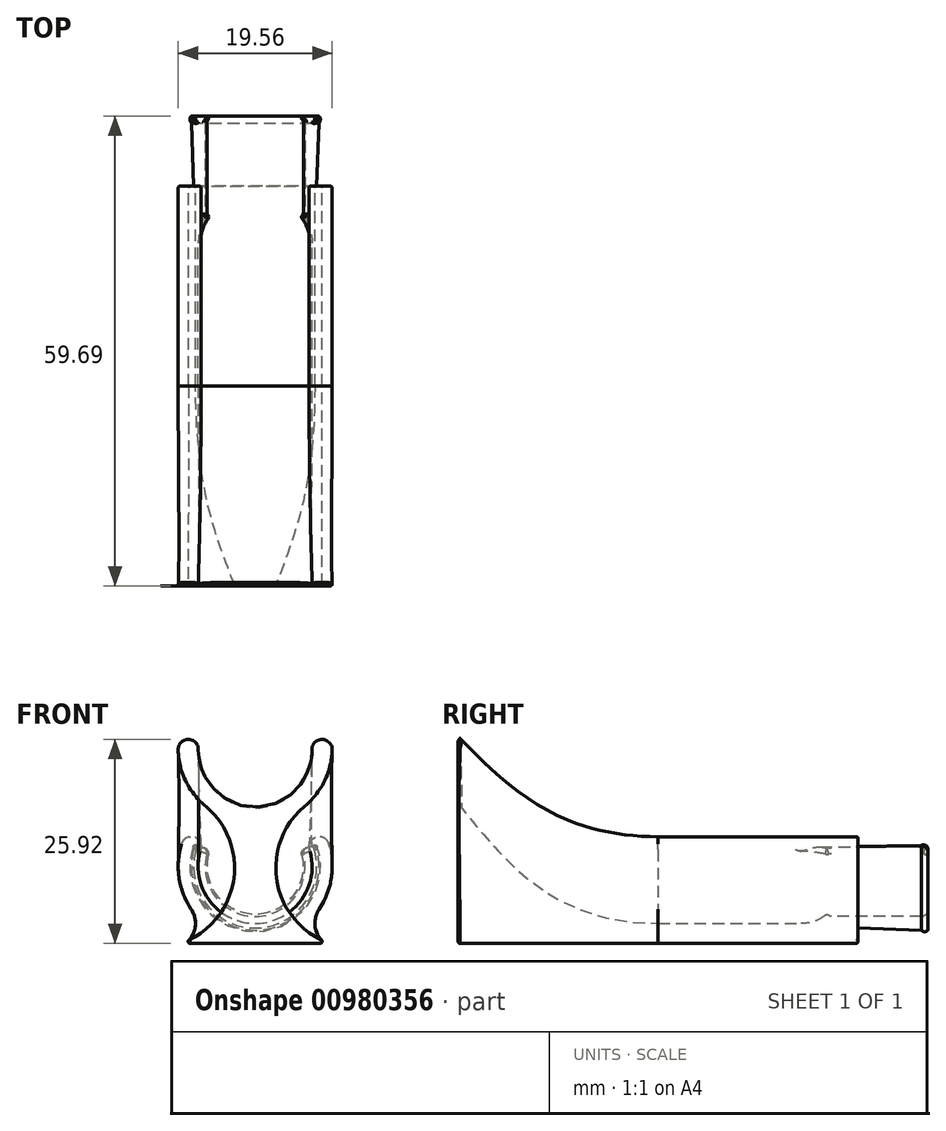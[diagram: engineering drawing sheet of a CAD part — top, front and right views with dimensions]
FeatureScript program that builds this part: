
annotation { "Feature Type Name" : "Feature", "Feature Type Description" : "" }
export const myFeature = defineFeature(function(context is Context, id is Id, definition is map)
    precondition{}
    {
        {
            var Q0;
            Q0=qCreatedBy(makeId("Front.planeOp"),FACE);
            var sketch = newSketch(context, id + "F0", { "sketchPlane" : qUnion([Q0])});
            skLineSegment(sketch, "E0", {"start": v(0, 0) * mm, "end": v(0, 2.54) * mm, "construction": true});
            skLineSegment(sketch, "E1", {"start": v(0, 0) * mm, "end": v(-8.23, 0) * mm});
            skArc(sketch, "E2", {"start": v(-6.91, 11.92) * mm, "mid": v(-5.83, 5.48) * mm, "end": v(0, 2.54) * mm});
            skArc(sketch, "E3", {"start": v(-6.91, 11.92) * mm, "mid": v(-7.75, 13.5) * mm, "end": v(-9.34, 12.67) * mm});
            skArc(sketch, "E4", {"start": v(-9.34, 12.67) * mm, "mid": v(-9.68, 8.37) * mm, "end": v(-8.12, 4.33) * mm});
            skArc(sketch, "E5", {"start": v(-8.42, 0.43) * mm, "mid": v(-7.6, 2.33) * mm, "end": v(-8.12, 4.33) * mm});
            skPoint(sketch, "E6.visualSharp", {"position": v(-8.9, 0) * mm});
            skArc(sketch, "E6.filletArc", {"start": v(-8.42, 0.43) * mm, "mid": v(-8.46, 0.15) * mm, "end": v(-8.23, 0) * mm});
            skPoint(sketch, "E7", {"position": v(-7.24, 9.78) * mm});
            skPoint(sketch, "E8", {"position": v(-6.86, 12.3) * mm});
            skArc(sketch, "E9.MirrorCS", {"start": v(6.91, 11.92) * mm, "mid": v(5.83, 5.48) * mm, "end": v(0, 2.54) * mm});
            skArc(sketch, "E10.MirrorCS", {"start": v(6.91, 11.92) * mm, "mid": v(7.75, 13.5) * mm, "end": v(9.34, 12.67) * mm});
            skArc(sketch, "E11.MirrorCS", {"start": v(9.34, 12.67) * mm, "mid": v(9.68, 8.37) * mm, "end": v(8.12, 4.33) * mm});
            skArc(sketch, "E12.MirrorCS", {"start": v(8.42, 0.43) * mm, "mid": v(7.6, 2.33) * mm, "end": v(8.12, 4.33) * mm});
            skLineSegment(sketch, "E13.MirrorCS", {"start": v(0, 0) * mm, "end": v(8.23, 0) * mm});
            skArc(sketch, "E14.MirrorCS", {"start": v(8.42, 0.43) * mm, "mid": v(8.46, 0.15) * mm, "end": v(8.23, 0) * mm});
            skSolve(sketch);
        }
        {
            var Q0;
            Q0=qSketchRegion(id+"F0",true);
            extrude(context, id + "F1", {"entities" : qUnion([Q0]), "depth" : 25.4 * mm, "offsetDistance" : 25.4 * mm});
        }
        {
            var Q0;
            Q0=makeQuery(id+"F1.opExtrude","CAP_FACE",FACE,{"disambiguationData":[OSD([sQuery(id+"F0.wireOp",EDGE,"E1"),sQuery(id+"F0.wireOp",EDGE,"E2"),sQuery(id+"F0.wireOp",EDGE,"E3"),sQuery(id+"F0.wireOp",EDGE,"E4"),sQuery(id+"F0.wireOp",EDGE,"E5"),sQuery(id+"F0.wireOp",EDGE,"E6.filletArc"),sQuery(id+"F0.wireOp",EDGE,"E9.MirrorCS"),sQuery(id+"F0.wireOp",EDGE,"E10.MirrorCS"),sQuery(id+"F0.wireOp",EDGE,"E11.MirrorCS"),sQuery(id+"F0.wireOp",EDGE,"E12.MirrorCS"),sQuery(id+"F0.wireOp",EDGE,"E13.MirrorCS"),sQuery(id+"F0.wireOp",EDGE,"E14.MirrorCS")])],"isStart":false});
            cPlane(context, id + "F2", {"entities" : qUnion([Q0]), "cplaneType" : CPlaneType.OFFSET, "offset" : 25.4 * mm, "width" : 152.4 * mm, "height" : 152.4 * mm});
        }
        {
            var Q0;
            Q0=qCreatedBy(id+"F2.planeOp",FACE);
            var sketch = newSketch(context, id + "F3", { "sketchPlane" : qUnion([Q0])});
            skLineSegment(sketch, "E15", {"start": v(0, 0) * mm, "end": v(0, 17.78) * mm, "construction": true});
            skLineSegment(sketch, "E16", {"start": v(8.26, 0) * mm, "end": v(-8.26, 0) * mm});
            skArc(sketch, "E17", {"start": v(-7.24, 25.02) * mm, "mid": v(0, 17.78) * mm, "end": v(7.24, 25.02) * mm});
            skArc(sketch, "E18", {"start": v(-7.24, 25.02) * mm, "mid": v(-8.5, 26.29) * mm, "end": v(-9.78, 25.02) * mm});
            skArc(sketch, "E19", {"start": v(-9.78, 25.02) * mm, "mid": v(-8.85, 20.86) * mm, "end": v(-6.24, 17.49) * mm});
            skArc(sketch, "E20", {"start": v(-8.36, 0.48) * mm, "mid": v(-2.64, 8.4) * mm, "end": v(-6.24, 17.49) * mm});
            skArc(sketch, "E21.filletArc", {"start": v(-8.36, 0.48) * mm, "mid": v(-8.5, 0.2) * mm, "end": v(-8.26, 0) * mm});
            skPoint(sketch, "E22", {"position": v(-7.24, 25.02) * mm});
            skArc(sketch, "E23.MirrorCS", {"start": v(7.24, 25.02) * mm, "mid": v(8.5, 26.29) * mm, "end": v(9.78, 25.02) * mm});
            skArc(sketch, "E24.MirrorCS", {"start": v(9.78, 25.02) * mm, "mid": v(8.85, 20.86) * mm, "end": v(6.24, 17.49) * mm});
            skArc(sketch, "E25.MirrorCS", {"start": v(8.36, 0.48) * mm, "mid": v(2.64, 8.4) * mm, "end": v(6.24, 17.49) * mm});
            skArc(sketch, "E26.MirrorCS", {"start": v(8.36, 0.48) * mm, "mid": v(8.5, 0.2) * mm, "end": v(8.26, 0) * mm});
            skSolve(sketch);
        }
        {
            var Q1;
            Q1=makeQuery(id+"F3.imprint","IMPRINT",FACE,{"disambiguationData":[TD([[makeQuery(id+"F3.imprint","IMPRINT",EDGE,{"derivedFrom":sQuery(id+"F3.wireOp",EDGE,"E16")}),-1.0]])]});
            var Q2;
            Q2=makeQuery(id+"F1.opExtrude","CAP_FACE",FACE,{"disambiguationData":[OSD([sQuery(id+"F0.wireOp",EDGE,"E1"),sQuery(id+"F0.wireOp",EDGE,"E2"),sQuery(id+"F0.wireOp",EDGE,"E3"),sQuery(id+"F0.wireOp",EDGE,"E4"),sQuery(id+"F0.wireOp",EDGE,"E5"),sQuery(id+"F0.wireOp",EDGE,"E6.filletArc"),sQuery(id+"F0.wireOp",EDGE,"E9.MirrorCS"),sQuery(id+"F0.wireOp",EDGE,"E10.MirrorCS"),sQuery(id+"F0.wireOp",EDGE,"E11.MirrorCS"),sQuery(id+"F0.wireOp",EDGE,"E12.MirrorCS"),sQuery(id+"F0.wireOp",EDGE,"E13.MirrorCS"),sQuery(id+"F0.wireOp",EDGE,"E14.MirrorCS")])],"isStart":false});
            loft(context, id + "F4", {"operationType" : NewBodyOperationType.ADD, "endCondition" : LoftEndDerivativeType.MATCH_TANGENT, "endMagnitude" : 1.5, "sheetProfilesArray" : [{ "sheetProfileEntities" : qUnion([Q1]) }, { "sheetProfileEntities" : qUnion([Q2]) }]});
        }
        {
            var Q0;
            Q0=makeQuery(id+"F4.opLoft","MID_CAP_EDGE",EDGE,{"disambiguationData":[OSD([sQuery(id+"F3.wireOp",EDGE,"E17"),sQuery(id+"F3.wireOp",EDGE,"E18"),sQuery(id+"F3.wireOp",EDGE,"E23.MirrorCS")])],"capPos":0.0});
            fillet(context, id + "F5", {"entities" : qUnion([Q0]), "radius" : 0.25 * mm, "tangentPropagation" : true, "allowEdgeOverflow" : false});
        }
        {
            var Q0;
            Q0=qCreatedBy(makeId("Right.planeOp"),FACE);
            var sketch = newSketch(context, id + "F6", { "sketchPlane" : qUnion([Q0])});
            skLineSegment(sketch, "E27", {"start": v(0, 9.78) * mm, "end": v(9.62, 9.78) * mm, "construction": true});
            skLineSegment(sketch, "E28", {"start": v(-4.19, 2.1) * mm, "end": v(8.02, 1.68) * mm});
            skLineSegment(sketch, "E29", {"start": v(-4.19, 2.1) * mm, "end": v(-4.19, 3.43) * mm});
            skLineSegment(sketch, "E30", {"start": v(-3.37, 3.43) * mm, "end": v(8.07, 3.43) * mm});
            skLineSegment(sketch, "E31", {"start": v(8.9, 3.43) * mm, "end": v(8.9, 1.65) * mm});
            skArc(sketch, "E32", {"start": v(8.9, 3.43) * mm, "mid": v(8.73, 3.67) * mm, "end": v(8.45, 3.6) * mm});
            skArc(sketch, "E33", {"start": v(-3.75, 3.6) * mm, "mid": v(-4.03, 3.67) * mm, "end": v(-4.19, 3.43) * mm});
            skPoint(sketch, "E34.visualSharp", {"position": v(-3.68, 3.43) * mm});
            skArc(sketch, "E34.filletArc", {"start": v(-3.75, 3.6) * mm, "mid": v(-3.57, 3.47) * mm, "end": v(-3.37, 3.43) * mm});
            skPoint(sketch, "E35.visualSharp", {"position": v(8.38, 3.43) * mm});
            skArc(sketch, "E35.filletArc", {"start": v(8.07, 3.43) * mm, "mid": v(8.28, 3.47) * mm, "end": v(8.45, 3.6) * mm});
            skArc(sketch, "E36", {"start": v(8.02, 1.68) * mm, "mid": v(8.45, 1.5) * mm, "end": v(8.9, 1.65) * mm});
            skLineSegment(sketch, "E37", {"start": v(8.02, 1.68) * mm, "end": v(8.57, 1.14) * mm, "construction": true});
            skLineSegment(sketch, "E38", {"start": v(8.02, 1.68) * mm, "end": v(8.9, 1.65) * mm});
            skSolve(sketch);
        }
        {
            var Q0;
            Q0=makeQuery(id+"F6.imprint","IMPRINT",FACE,{"disambiguationData":[TD([[makeQuery(id+"F6.imprint","IMPRINT",EDGE,{"derivedFrom":sQuery(id+"F6.wireOp",EDGE,"E28")}),1.0]])]});
            var Q1;
            Q1=makeQuery(id+"F6.imprint","IMPRINT",FACE,{"disambiguationData":[TD([[makeQuery(id+"F6.imprint","IMPRINT",EDGE,{"derivedFrom":sQuery(id+"F6.wireOp",EDGE,"E36")}),1.0]])]});
            var Q2;
            Q2=sQuery(id+"F6.wireOp",EDGE,"E27");
            revolve(context, id + "F7", {"operationType" : NewBodyOperationType.ADD, "surfaceOperationType" : NewSurfaceOperationType.NEW, "entities" : qUnion([Q0, Q1]), "axis" : qUnion([Q2]), "revolveType" : RevolveType.SYMMETRIC, "angle" : 220 * degree});
        }
        {
            var Q0;
            Q0=makeQuery(id+"F7.boolean.opBoolean","INTERSECT",EDGE,{"derivedFrom":[makeQuery(id+"F1.opExtrude","SWEPT_FACE",FACE,{"disambiguationData":[OSD([sQuery(id+"F0.wireOp",EDGE,"E2"),sQuery(id+"F0.wireOp",EDGE,"E9.MirrorCS")])]}),makeQuery(id+"F7.opRevolve","SWEPT_FACE",FACE,{"disambiguationData":[OSD([sQuery(id+"F6.wireOp",EDGE,"E29")])]})]});
            fillet(context, id + "F8", {"entities" : qUnion([Q0]), "radius" : 5.08 * mm, "tangentPropagation" : true, "allowEdgeOverflow" : false});
        }
        {
            var Q0;
            Q0=makeQuery(id+"F7qckbc8QIdeTG0_1.boolean.opBoolean","INTERSECT",EDGE,{"derivedFrom":[makeQuery(id+"F1.opExtrude","SWEPT_FACE",FACE,{"disambiguationData":[OSD([sQuery(id+"F0.wireOp",EDGE,"E3")])]}),makeQuery(id+"F7qckbc8QIdeTG0_1.opRevolve","SWEPT_FACE",FACE,{"disambiguationData":[OSD([sQuery(id+"F6.wireOp",EDGE,"8610247d-b99b-46d6-847c-e21840621b50")])]})]});
            var Q1;
            Q1=makeQuery(id+"F7qckbc8QIdeTG0_1.boolean.opBoolean","INTERSECT",EDGE,{"derivedFrom":[makeQuery(id+"F1.opExtrude","SWEPT_FACE",FACE,{"disambiguationData":[OSD([sQuery(id+"F0.wireOp",EDGE,"E10.MirrorCS")])]}),makeQuery(id+"F7qckbc8QIdeTG0_1.opRevolve","SWEPT_FACE",FACE,{"disambiguationData":[OSD([sQuery(id+"F6.wireOp",EDGE,"8610247d-b99b-46d6-847c-e21840621b50")])]})]});
            var Q2;
            Q2=makeQuery(id+"F7.opRevolve","CAP_EDGE",EDGE,{"disambiguationData":[OSD([sQuery(id+"F6.wireOp",EDGE,"E30")])],"isStart":false});
            var Q3;
            Q3=makeQuery(id+"F7.opRevolve","CAP_EDGE",EDGE,{"disambiguationData":[OSD([sQuery(id+"F6.wireOp",EDGE,"E30")])],"isStart":true});
            fillet(context, id + "F9", {"entities" : qUnion([Q0, Q1, Q2, Q3]), "radius" : 0.64 * mm, "tangentPropagation" : true, "allowEdgeOverflow" : false});
        }
        {
            var Q0;
            Q0=makeQuery(id+"F7.opRevolve","CAP_EDGE",EDGE,{"disambiguationData":[OSD([sQuery(id+"F6.wireOp",EDGE,"E28")])],"isStart":false});
            var Q1;
            Q1=makeQuery(id+"F7.opRevolve","CAP_EDGE",EDGE,{"disambiguationData":[OSD([sQuery(id+"F6.wireOp",EDGE,"E28")])],"isStart":true});
            fillet(context, id + "F10", {"entities" : qUnion([Q0, Q1]), "radius" : 0.46 * mm, "tangentPropagation" : true, "allowEdgeOverflow" : false});
        }
        {
            var Q0;
            Q0=makeQuery(id+"F7qckbc8QIdeTG0_1.boolean.opBoolean","INTERSECT",EDGE,{"derivedFrom":[makeQuery(id+"F1.opExtrude","CAP_FACE",FACE,{"disambiguationData":[OSD([sQuery(id+"F0.wireOp",EDGE,"E1"),sQuery(id+"F0.wireOp",EDGE,"E2"),sQuery(id+"F0.wireOp",EDGE,"E3"),sQuery(id+"F0.wireOp",EDGE,"E4"),sQuery(id+"F0.wireOp",EDGE,"E5"),sQuery(id+"F0.wireOp",EDGE,"E6.filletArc"),sQuery(id+"F0.wireOp",EDGE,"E9.MirrorCS"),sQuery(id+"F0.wireOp",EDGE,"E10.MirrorCS"),sQuery(id+"F0.wireOp",EDGE,"E11.MirrorCS"),sQuery(id+"F0.wireOp",EDGE,"E12.MirrorCS"),sQuery(id+"F0.wireOp",EDGE,"E13.MirrorCS"),sQuery(id+"F0.wireOp",EDGE,"E14.MirrorCS")])],"isStart":false}),makeQuery(id+"F7qckbc8QIdeTG0_1.opRevolve","SWEPT_FACE",FACE,{"disambiguationData":[OSD([sQuery(id+"F6.wireOp",EDGE,"8610247d-b99b-46d6-847c-e21840621b50")])]})]});
            var Q1;
            Q1=makeQuery(id+"F7qckbc8QIdeTG0_1.boolean.opBoolean","INTERSECT",EDGE,{"derivedFrom":[makeQuery(id+"F1.opExtrude","SWEPT_FACE",FACE,{"disambiguationData":[OSD([sQuery(id+"F0.wireOp",EDGE,"E2"),sQuery(id+"F0.wireOp",EDGE,"E9.MirrorCS")])]}),makeQuery(id+"F7qckbc8QIdeTG0_1.opRevolve","SWEPT_FACE",FACE,{"disambiguationData":[OSD([sQuery(id+"F6.wireOp",EDGE,"0048d4bb-88ac-4f56-85f1-9bb627bb2a38")])]})]});
            var Q2;
            Q2=makeQuery(id+"F7.opRevolve","SWEPT_EDGE",EDGE,{"disambiguationData":[OSD([sQuery(id+"F6.wireOp",EDGE,"E30"),sQuery(id+"F6.wireOp",EDGE,"E31")])]});
            var Q3;
            Q3=makeQuery(id+"F1.opExtrude","CAP_EDGE",EDGE,{"disambiguationData":[OSD([sQuery(id+"F0.wireOp",EDGE,"E4")])],"isStart":true});
            var Q4;
            Q4=makeQuery(id+"F7.boolean.opBoolean","INTERSECT",EDGE,{"derivedFrom":[makeQuery(id+"F1.opExtrude","SWEPT_FACE",FACE,{"disambiguationData":[OSD([sQuery(id+"F0.wireOp",EDGE,"E2"),sQuery(id+"F0.wireOp",EDGE,"E9.MirrorCS")])]}),makeQuery(id+"F7.opRevolve","SWEPT_FACE",FACE,{"disambiguationData":[OSD([sQuery(id+"F6.wireOp",EDGE,"E29")])]})]});
            var Q5;
            Q5=makeQuery(id+"FH2piJS7uuTGJ2u_1.opExtrude","CAP_EDGE",EDGE,{"disambiguationData":[OSD([sQuery(id+"FoCLsh66cKFiKgl_1.wireOp",EDGE,"11dVqFUu-e9aY-AeWq-O7nq-crDflKvgFnvz.left")])],"isStart":true});
            var Q6;
            Q6=makeQuery(id+"FH2piJS7uuTGJ2u_1.opExtrude","CAP_EDGE",EDGE,{"disambiguationData":[OSD([sQuery(id+"FoCLsh66cKFiKgl_1.wireOp",EDGE,"11dVqFUu-e9aY-AeWq-O7nq-crDflKvgFnvz.right")])],"isStart":true});
            var Q7;
            Q7=makeQuery(id+"FH2piJS7uuTGJ2u_1.opExtrude","CAP_EDGE",EDGE,{"disambiguationData":[OSD([sQuery(id+"FoCLsh66cKFiKgl_1.wireOp",EDGE,"11dVqFUu-e9aY-AeWq-O7nq-crDflKvgFnvz.top")])],"isStart":true});
            var Q8;
            Q8=makeQuery(id+"FRpYH6i3VNikOXj_1.boolean.opBoolean","COPY",EDGE,{"derivedFrom":makeQuery(id+"FRpYH6i3VNikOXj_1.opExtrude","CAP_EDGE",EDGE,{"disambiguationData":[OSD([sQuery(id+"FoCLsh66cKFiKgl_1.wireOp",EDGE,"htWPkWeC-bwWN-7SjK-EXkN-T3KBYyp8dpbN.right")])],"isStart":true})});
            var Q9;
            Q9=makeQuery(id+"FRpYH6i3VNikOXj_1.boolean.opBoolean","COPY",EDGE,{"derivedFrom":makeQuery(id+"FRpYH6i3VNikOXj_1.opExtrude","CAP_EDGE",EDGE,{"disambiguationData":[OSD([sQuery(id+"FoCLsh66cKFiKgl_1.wireOp",EDGE,"htWPkWeC-bwWN-7SjK-EXkN-T3KBYyp8dpbN.top")])],"isStart":true})});
            var Q10;
            Q10=makeQuery(id+"FRpYH6i3VNikOXj_1.boolean.opBoolean","COPY",EDGE,{"derivedFrom":makeQuery(id+"FRpYH6i3VNikOXj_1.opExtrude","CAP_EDGE",EDGE,{"disambiguationData":[OSD([sQuery(id+"FoCLsh66cKFiKgl_1.wireOp",EDGE,"htWPkWeC-bwWN-7SjK-EXkN-T3KBYyp8dpbN.left")])],"isStart":true})});
            fillet(context, id + "F11", {"entities" : qUnion([Q0, Q1, Q2, Q3, Q4, Q5, Q6, Q7, Q8, Q9, Q10]), "radius" : 0.25 * mm, "tangentPropagation" : true, "allowEdgeOverflow" : false});
        }
        {
            var Q0;
            Q0=makeQuery(id+"F7.opRevolve","SWEPT_EDGE",EDGE,{"disambiguationData":[OSD([sQuery(id+"F6.wireOp",EDGE,"E31"),sQuery(id+"F6.wireOp",EDGE,"E36"),sQuery(id+"F6.wireOp",EDGE,"E38")])]});
            var Q1;
            Q1=makeQuery(id+"Fgvb5MgpSLeRp5C_1.boolean.opBoolean","COPY",EDGE,{"derivedFrom":makeQuery(id+"Fgvb5MgpSLeRp5C_1.opRevolve","SWEPT_EDGE",EDGE,{"disambiguationData":[OSD([sQuery(id+"F6.wireOp",EDGE,"8610247d-b99b-46d6-847c-e21840621b50"),sQuery(id+"F6.wireOp",EDGE,"gjB7T6E9-VnRk-seKC-vIAh-jFUWnk6iz1lL"),sQuery(id+"F6.wireOp",EDGE,"yuIz4UM6-47C7-kCJn-7ROk-OIwva0U0usmc")])]})});
            fillet(context, id + "F12", {"entities" : qUnion([Q0, Q1]), "radius" : 0.25 * mm, "tangentPropagation" : true, "allowEdgeOverflow" : false});
        }
    });
